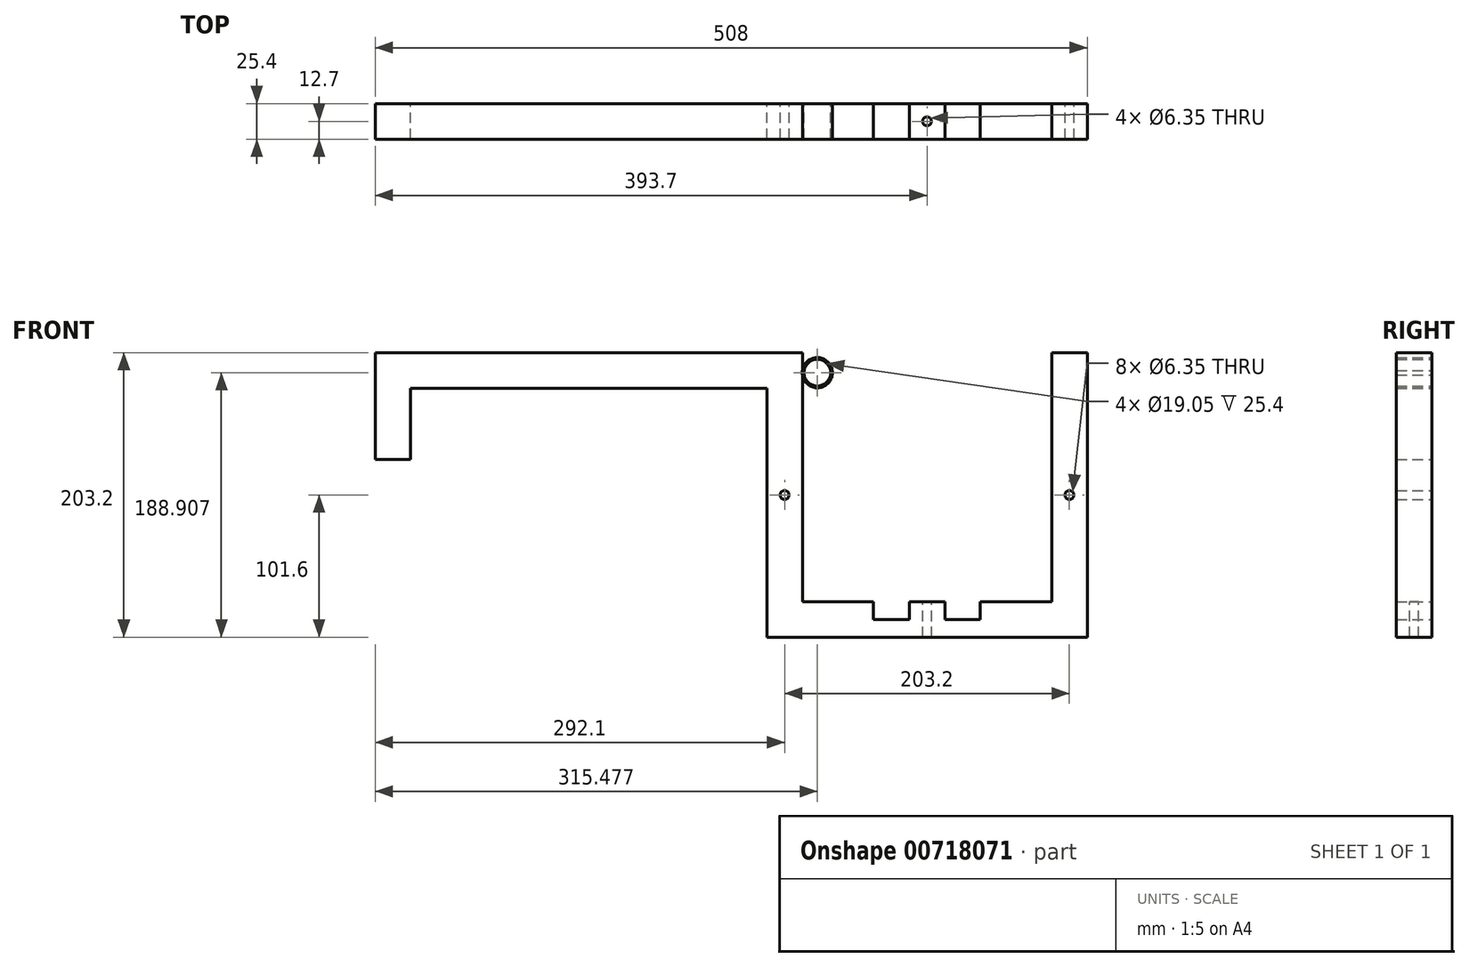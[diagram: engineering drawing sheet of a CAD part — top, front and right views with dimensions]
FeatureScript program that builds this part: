
annotation { "Feature Type Name" : "Feature", "Feature Type Description" : "" }
export const myFeature = defineFeature(function(context is Context, id is Id, definition is map)
    precondition{}
    {
        {
            var Q0;
            Q0=qCreatedBy(makeId("Front.planeOp"),FACE);
            var sketch = newSketch(context, id + "F0", { "sketchPlane" : qUnion([Q0])});
            skLineSegment(sketch, "E0.bottom", {"start": v(127, -12.7) * mm, "end": v(-127, -12.7) * mm});
            skLineSegment(sketch, "E0.top", {"start": v(127, 12.7) * mm, "end": v(-127, 12.7) * mm});
            skLineSegment(sketch, "E0.left", {"start": v(127, -12.7) * mm, "end": v(127, 12.7) * mm});
            skLineSegment(sketch, "E0.right", {"start": v(-127, -12.7) * mm, "end": v(-127, 12.7) * mm});
            skPoint(sketch, "E0.middle", {"position": v(0, 0) * mm});
            skLineSegment(sketch, "E1.bottom", {"start": v(-127, 12.7) * mm, "end": v(-152.4, 12.7) * mm});
            skLineSegment(sketch, "E1.top", {"start": v(-127, -63.5) * mm, "end": v(-152.4, -63.5) * mm});
            skLineSegment(sketch, "E1.left", {"start": v(-127, 12.7) * mm, "end": v(-127, -63.5) * mm});
            skLineSegment(sketch, "E1.right", {"start": v(-152.4, 12.7) * mm, "end": v(-152.4, -63.5) * mm});
            skLineSegment(sketch, "E2.bottom", {"start": v(127, 12.7) * mm, "end": v(152.4, 12.7) * mm});
            skLineSegment(sketch, "E2.top", {"start": v(127, -190.5) * mm, "end": v(152.4, -190.5) * mm});
            skLineSegment(sketch, "E2.left", {"start": v(127, 12.7) * mm, "end": v(127, -190.5) * mm});
            skLineSegment(sketch, "E2.right", {"start": v(152.4, 12.7) * mm, "end": v(152.4, -190.5) * mm});
            skLineSegment(sketch, "E3.bottom", {"start": v(152.4, -190.5) * mm, "end": v(330.2, -190.5) * mm});
            skLineSegment(sketch, "E3.top", {"start": v(152.4, -165.1) * mm, "end": v(203.2, -165.1) * mm});
            skLineSegment(sketch, "E3.left", {"start": v(152.4, -190.5) * mm, "end": v(152.4, -165.1) * mm});
            skLineSegment(sketch, "E3.right", {"start": v(330.2, -190.5) * mm, "end": v(330.2, -165.1) * mm});
            skLineSegment(sketch, "E4.bottom", {"start": v(330.2, -190.5) * mm, "end": v(355.6, -190.5) * mm});
            skLineSegment(sketch, "E4.top", {"start": v(330.2, 12.7) * mm, "end": v(355.6, 12.7) * mm});
            skLineSegment(sketch, "E4.left", {"start": v(330.2, -190.5) * mm, "end": v(330.2, 12.7) * mm});
            skLineSegment(sketch, "E4.right", {"start": v(355.6, -190.5) * mm, "end": v(355.6, 12.7) * mm});
            skLineSegment(sketch, "E5.top", {"start": v(203.2, -177.8) * mm, "end": v(228.6, -177.8) * mm});
            skLineSegment(sketch, "E5.left", {"start": v(203.2, -165.1) * mm, "end": v(203.2, -177.8) * mm});
            skLineSegment(sketch, "E5.right", {"start": v(228.6, -165.1) * mm, "end": v(228.6, -177.8) * mm});
            skLineSegment(sketch, "E6.trimOffspring", {"start": v(228.6, -165.1) * mm, "end": v(254, -165.1) * mm});
            skLineSegment(sketch, "E7.top", {"start": v(279.4, -177.8) * mm, "end": v(254, -177.8) * mm});
            skLineSegment(sketch, "E7.left", {"start": v(279.4, -165.1) * mm, "end": v(279.4, -177.8) * mm});
            skLineSegment(sketch, "E7.right", {"start": v(254, -165.1) * mm, "end": v(254, -177.8) * mm});
            skCircle(sketch, "E8", {"center": v(139.7, -88.9) * mm, "radius": 3.17 * mm});
            skPoint(sketch, "E8.centerSnap0", {"position": v(139.7, 12.7) * mm});
            skCircle(sketch, "E9", {"center": v(342.9, -88.9) * mm, "radius": 3.18 * mm});
            skPoint(sketch, "E9.centerSnap0", {"position": v(342.9, 12.7) * mm});
            skCircle(sketch, "E10", {"center": v(163.08, -1.6) * mm, "radius": 10.8 * mm});
            skPoint(sketch, "E10.first.point", {"position": v(152.4, 0) * mm});
            skPoint(sketch, "E10.second.point", {"position": v(173.75, 0) * mm});
            skPoint(sketch, "E10.third.point", {"position": v(164.36, 9.13) * mm});
            skCircle(sketch, "E11", {"center": v(163.08, -1.6) * mm, "radius": 9.53 * mm});
            skLineSegment(sketch, "E12.trimOffspring", {"start": v(279.4, -165.1) * mm, "end": v(330.2, -165.1) * mm});
            skSolve(sketch);
        }
        {
            var Q0;
            {var subQ0=makeQuery(id+"F0.imprint","IMPRINT",EDGE,{"derivedFrom":sQuery(id+"F0.wireOp",EDGE,"E3.right")});var subQ1=sQuery(id+"F0.wireOp",EDGE,"E3.bottom");var subQ2=sQuery(id+"F0.wireOp",EDGE,"E2.right");var subQ7=sQuery(id+"F0.wireOp",EDGE,"E10");var subQ8=makeQuery(id+"F0.imprint","INTERSECT",VERTEX,{"disambiguationData":[OD(0.0)],"derivedFrom":[subQ2,subQ7]});var subQ10=makeQuery(id+"F0.imprint","IMPRINT",EDGE,{"disambiguationData":[TD([[subQ8,1.0]])],"derivedFrom":subQ2});var subQ12=makeQuery(id+"F0.imprint","IMPRINT",EDGE,{"derivedFrom":sQuery(id+"F0.wireOp",EDGE,"E0.left")});var subQ13=makeQuery(id+"F0.imprint","IMPRINT",EDGE,{"derivedFrom":sQuery(id+"F0.wireOp",EDGE,"E0.right")});Q0=qUnion([makeQuery(id+"F0.imprint","IMPRINT",FACE,{"disambiguationData":[TD([[subQ12,-1.0]])]}),makeQuery(id+"F0.imprint","IMPRINT",FACE,{"disambiguationData":[TD([[makeQuery(id+"F0.imprint","IMPRINT",EDGE,{"derivedFrom":sQuery(id+"F0.wireOp",EDGE,"E11")}),-1.0]])]}),makeQuery(id+"F0.imprint","IMPRINT",FACE,{"disambiguationData":[TD([[subQ13,1.0]])]}),makeQuery(id+"F0.imprint","IMPRINT",FACE,{"disambiguationData":[TD([[makeQuery(id+"F0.imprint","IMPRINT",EDGE,{"derivedFrom":sQuery(id+"F0.wireOp",EDGE,"E0.bottom")}),-1.0]])]}),makeQuery(id+"F0.imprint","IMPRINT",FACE,{"disambiguationData":[TD([[subQ10,-1.0]])]}),makeQuery(id+"F0.imprint","IMPRINT",FACE,{"disambiguationData":[TD([[makeQuery(id+"F0.imprint","IMPRINT",EDGE,{"derivedFrom":subQ1}),1.0]])]}),makeQuery(id+"F0.imprint","IMPRINT",FACE,{"disambiguationData":[TD([[subQ0,-1.0]])]})]);}
            extrude(context, id + "F1", {"entities" : qUnion([Q0]), "depth" : 25.4 * mm, "offsetDistance" : 25.4 * mm});
        }
        {
            var Q0;
            Q0=makeQuery(id+"F1.opExtrude","SWEPT_FACE",FACE,{"disambiguationData":[OSD([sQuery(id+"F0.wireOp",EDGE,"E6.trimOffspring")])]});
            var sketch = newSketch(context, id + "F2", { "sketchPlane" : qUnion([Q0])});
            skCircle(sketch, "E13", {"center": v(241.3, -12.7) * mm, "radius": 3.18 * mm});
            skPoint(sketch, "E13.centerSnap0", {"position": v(228.6, -12.7) * mm});
            skPoint(sketch, "E13.centerSnap1", {"position": v(241.3, 0) * mm});
            skSolve(sketch);
        }
        {
            var Q0;
            Q0 = qSketchRegion(id + "F2", true);
            extrude(context, id + "F3", {"entities" : qUnion([Q0]), "operationType" : NewBodyOperationType.REMOVE, "oppositeDirection" : true, "depth" : 25.4 * mm, "offsetDistance" : 25.4 * mm});
        }
    });
